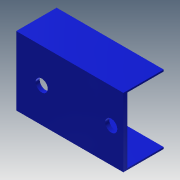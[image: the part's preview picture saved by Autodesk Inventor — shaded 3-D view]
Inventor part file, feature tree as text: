
AUTODESK INVENTOR PART (.ipt)
format: ipt  version: 2013 (Build 170138000, 138)  size: 157,696 bytes
history: native  units: mm
features: extrude x9, sketch x9
ambient origin geometry x8: Origin, YZ Plane, XZ Plane, XY Plane, X Axis, Y Axis, Z Axis, Center Point
bodies: Solid1 (feature_tree)
feature tree (18):
  extrude  "Extrusion1"  Depth=17.0mm
  extrude  "Extrusion2"  Depth=24.7mm
  extrude  "Extrusion3"  Depth=9.0mm TaperAngle=0.0deg
  extrude  "Extrusion4"  Depth=3.0mm
  extrude  "Extrusion5"  Depth=3.0mm
  extrude  "Extrusion6"  Depth=2.0mm TaperAngle=0.0deg
  extrude  "Extrusion7"  Depth=2.0mm
  extrude  "Extrusion8"  Depth=3.0mm
  extrude  "Extrusion9"  Depth=3.3mm
  sketch  "Sketch1"  dims[d0=24.7mm d1=17.0mm]
  sketch  "Sketch2"  dims[d2=10.0mm d3=0.0mm d4=24.7mm]
  sketch  "Sketch3"  dims[d5=16.2mm d6=9.0mm d7=0.0mm]
  sketch  "Sketch4"  dims[d8=3.0mm d9=3.0mm]
  sketch  "Sketch5"  dims[d10=3.0mm d11=3.0mm]
  sketch  "Sketch6"  dims[d12=1.0mm d13=0.0mm d14=2.0mm d15=0.0mm]
  sketch  "Sketch7"  dims[d16=0.2mm d17=0.0mm d18=2.0mm]
  sketch  "Sketch8"  dims[d19=2.0mm d20=3.0mm]
  sketch  "Sketch9"  dims[d21=1.0mm d22=0.0mm d29=3.3mm d30=3.0mm d31=3.0mm d32=1.0mm d33=0.0mm d34=0.1mm d35=0.1mm d36=1.0mm d37=0.0mm d38=3.0mm d39=3.0mm d40=1.0mm d41=0.0mm]
